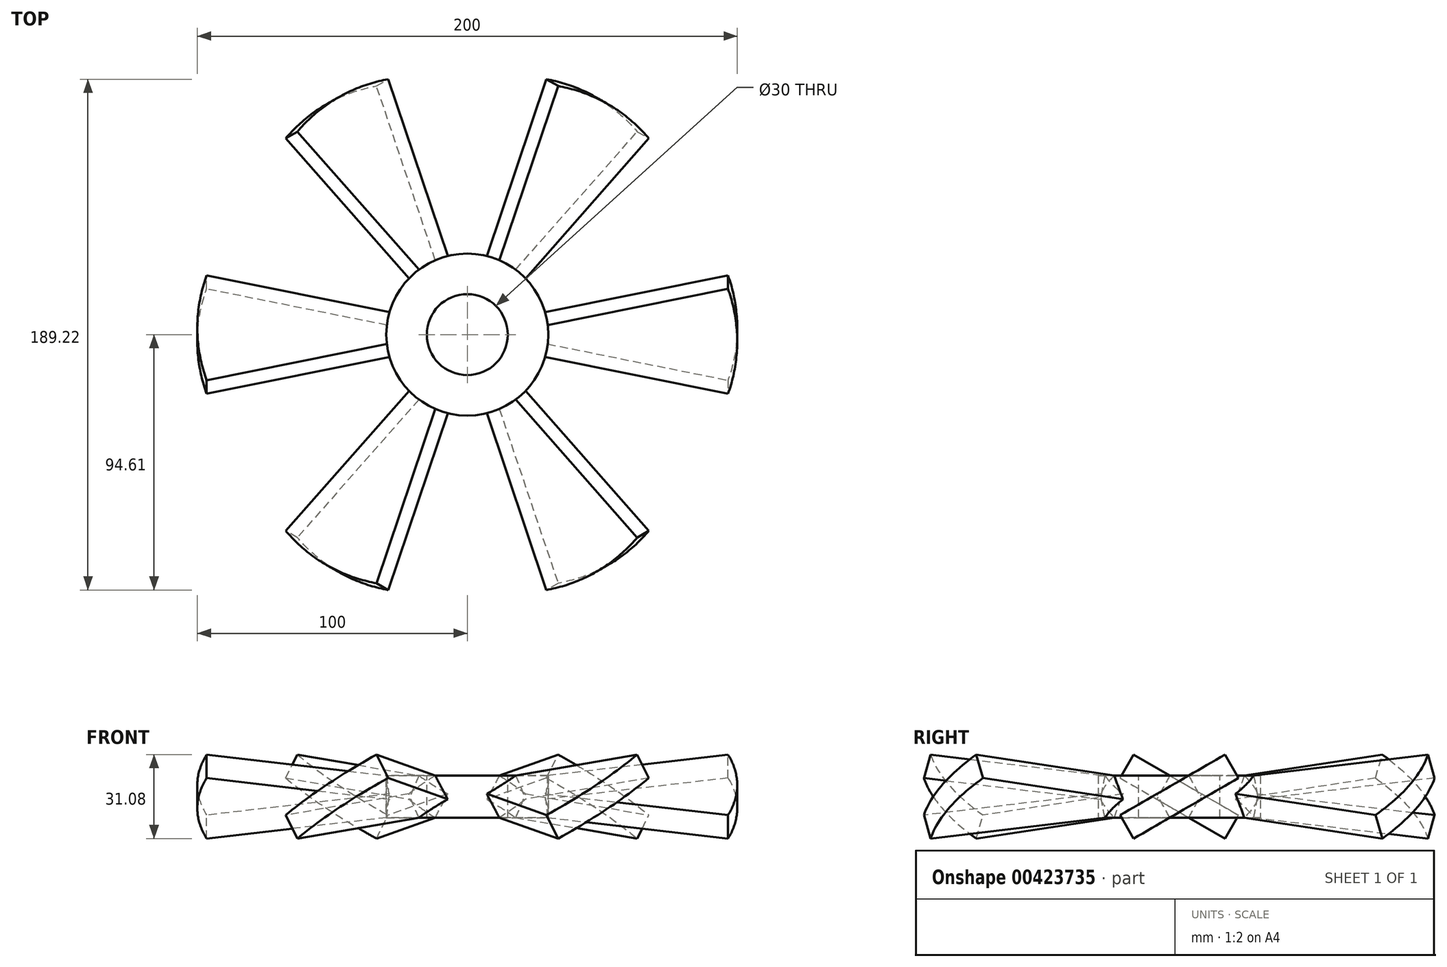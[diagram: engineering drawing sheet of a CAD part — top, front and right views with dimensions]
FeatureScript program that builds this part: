
annotation { "Feature Type Name" : "Feature", "Feature Type Description" : "" }
export const myFeature = defineFeature(function(context is Context, id is Id, definition is map)
    precondition{}
    {
        {
            var Q0;
            Q0=qCreatedBy(makeId("Top.planeOp"),FACE);
            var sketch = newSketch(context, id + "F0", { "sketchPlane" : qUnion([Q0])});
            skCircle(sketch, "E0", {"center": v(0, 0) * mm, "radius": 30 * mm});
            skSolve(sketch);
        }
        {
            var Q0;
            Q0=qCreatedBy(makeId("Top.planeOp"),FACE);
            var sketch = newSketch(context, id + "F1", { "sketchPlane" : qUnion([Q0])});
            skArc(sketch, "E1", {"start": v(96.6, -25.88) * mm, "mid": v(100, 0) * mm, "end": v(96.6, 25.88) * mm});
            skLineSegment(sketch, "E2", {"start": v(0, 0) * mm, "end": v(96.6, 25.88) * mm});
            skLineSegment(sketch, "E3.MirrorCS", {"start": v(0, 0) * mm, "end": v(96.6, -25.88) * mm});
            skLineSegment(sketch, "E4", {"start": v(0, 0) * mm, "end": v(160.9, 0) * mm, "construction": true});
            skSolve(sketch);
        }
        {
            var Q0;
            Q0=sQuery(id+"F1.wireOp",EDGE,"E4");
            cPlane(context, id + "F2", {"entities" : qUnion([Q0]), "cplaneType" : CPlaneType.LINE_ANGLE, "offset" : 25 * mm, "angle" : 60 * degree, "oppositeDirection" : true, "width" : 150 * mm, "height" : 150 * mm});
        }
        {
            var Q0;
            Q0=qCreatedBy(id+"F2.planeOp",FACE);
            var sketch = newSketch(context, id + "F3", { "sketchPlane" : qUnion([Q0])});
            skLineSegment(sketch, "E5.0.0", {"start": v(96.6, -22.41) * mm, "end": v(0, 0) * mm});
            skLineSegment(sketch, "E5.0.1", {"start": v(0, 0) * mm, "end": v(96.6, 22.41) * mm});
            skEllipticalArc(sketch, "E5.0.2", {});
            const initialGuessF3  = {"E5.0.2": [0, 0, -1, 0, 0.1, 0.08660254037844387, 2.8797932657906435, 3.4033920413889427]};
            skSetInitialGuess(sketch, initialGuessF3);
            skSolve(sketch);
        }
        {
            var Q0;
            Q0=makeQuery(id+"F3.imprint","IMPRINT",FACE,{"disambiguationData":[TD([[makeQuery(id+"F3.imprint","IMPRINT",EDGE,{"derivedFrom":sQuery(id+"F3.wireOp",EDGE,"E5.0.0")}),-1.0]])]});
            extrude(context, id + "F4", {"entities" : qUnion([Q0]), "endBound" : BoundingType.SYMMETRIC, "depth" : 10 * mm});
        }
        {
            var Q0;
            Q0=makeQuery(id+"F0.imprint","IMPRINT",FACE,{"disambiguationData":[TD([[makeQuery(id+"F0.imprint","IMPRINT",EDGE,{"derivedFrom":sQuery(id+"F0.wireOp",EDGE,"E0")}),1.0]])]});
            extrude(context, id + "F5", {"entities" : qUnion([Q0]), "operationType" : NewBodyOperationType.REMOVE, "endBound" : BoundingType.SYMMETRIC, "oppositeDirection" : true, "depth" : 25 * mm});
        }
        {
            var Q0;
            Q0=makeQuery(id+"F0.imprint","IMPRINT",FACE,{"disambiguationData":[TD([[makeQuery(id+"F0.imprint","IMPRINT",EDGE,{"derivedFrom":sQuery(id+"F0.wireOp",EDGE,"E0")}),1.0]])]});
            var Q1;
            {var subQ0=sQuery(id+"F3.wireOp",EDGE,"E5.0.0");Q1=makeQuery(id+"F5.boolean.opBoolean","INTERSECT",VERTEX,{"derivedFrom":[makeQuery(id+"F4.opExtrude","SWEPT_FACE",FACE,{"disambiguationData":[OSD([subQ0])]}),makeQuery(id+"F4.opExtrude","CAP_FACE",FACE,{"disambiguationData":[OSD([subQ0,sQuery(id+"F3.wireOp",EDGE,"E5.0.1"),sQuery(id+"F3.wireOp",EDGE,"E5.0.2")])],"isStart":true}),makeQuery(id+"F5.opExtrude","SWEPT_FACE",FACE,{"disambiguationData":[OSD([sQuery(id+"F0.wireOp",EDGE,"E0")])]})]});}
            var Q2;
            {var subQ0=sQuery(id+"F3.wireOp",EDGE,"E5.0.1");Q2=makeQuery(id+"F5.boolean.opBoolean","INTERSECT",VERTEX,{"derivedFrom":[makeQuery(id+"F4.opExtrude","CAP_FACE",FACE,{"disambiguationData":[OSD([sQuery(id+"F3.wireOp",EDGE,"E5.0.0"),subQ0,sQuery(id+"F3.wireOp",EDGE,"E5.0.2")])],"isStart":false}),makeQuery(id+"F4.opExtrude","SWEPT_FACE",FACE,{"disambiguationData":[OSD([subQ0])]}),makeQuery(id+"F5.opExtrude","SWEPT_FACE",FACE,{"disambiguationData":[OSD([sQuery(id+"F0.wireOp",EDGE,"E0")])]})]});}
            extrude(context, id + "F6", {"entities" : qUnion([Q0]), "endBound" : BoundingType.UP_TO_VERTEX, "endBoundEntityVertex" : qUnion([Q1]), "depth" : 25 * mm, "hasSecondDirection" : true, "secondDirectionBound" : SecondDirectionBoundingType.UP_TO_VERTEX, "secondDirectionOppositeDirection" : true, "secondDirectionBoundEntityVertex" : qUnion([Q2]), "secondDirectionDepth" : 25 * mm});
        }
        {
            var Q0;
            Q0=qCreatedBy(makeId("Right.planeOp"),FACE);
            var sketch = newSketch(context, id + "F7", { "sketchPlane" : qUnion([Q0])});
            skLineSegment(sketch, "E6", {"start": v(0, 0) * mm, "end": v(0, 48.42) * mm, "construction": true});
            skSolve(sketch);
        }
        {
            var Q0;
            Q0=makeQuery(id+"F4.opExtrude","SWEPT_BODY",BODY,{"disambiguationData":[OSD([sQuery(id+"F3.wireOp",EDGE,"E5.0.0"),sQuery(id+"F3.wireOp",EDGE,"E5.0.1"),sQuery(id+"F3.wireOp",EDGE,"E5.0.2")])]});
            var Q1;
            Q1=sQuery(id+"F7.wireOp",EDGE,"E6");
            circularPattern(context, id + "F8", {"entities" : qUnion([Q0]), "axis" : qUnion([Q1]), "angle" : 360 * degree, "instanceCount" : 6, "equalSpace" : true});
        }
        {
            var Q0;
            Q0=makeQuery(id+"F6.opExtrude","CAP_FACE",FACE,{"disambiguationData":[OSD([sQuery(id+"F0.wireOp",EDGE,"E0")])],"isStart":false});
            var sketch = newSketch(context, id + "F9", { "sketchPlane" : qUnion([Q0])});
            skCircle(sketch, "E7", {"center": v(0, 0) * mm, "radius": 15 * mm});
            skSolve(sketch);
        }
        {
            var Q0;
            Q0=makeQuery(id+"F9.imprint","IMPRINT",FACE,{"disambiguationData":[TD([[makeQuery(id+"F9.imprint","IMPRINT",EDGE,{"derivedFrom":sQuery(id+"F9.wireOp",EDGE,"E7")}),1.0]])]});
            extrude(context, id + "F10", {"entities" : qUnion([Q0]), "operationType" : NewBodyOperationType.REMOVE, "oppositeDirection" : true, "depth" : 25 * mm});
        }
    });
